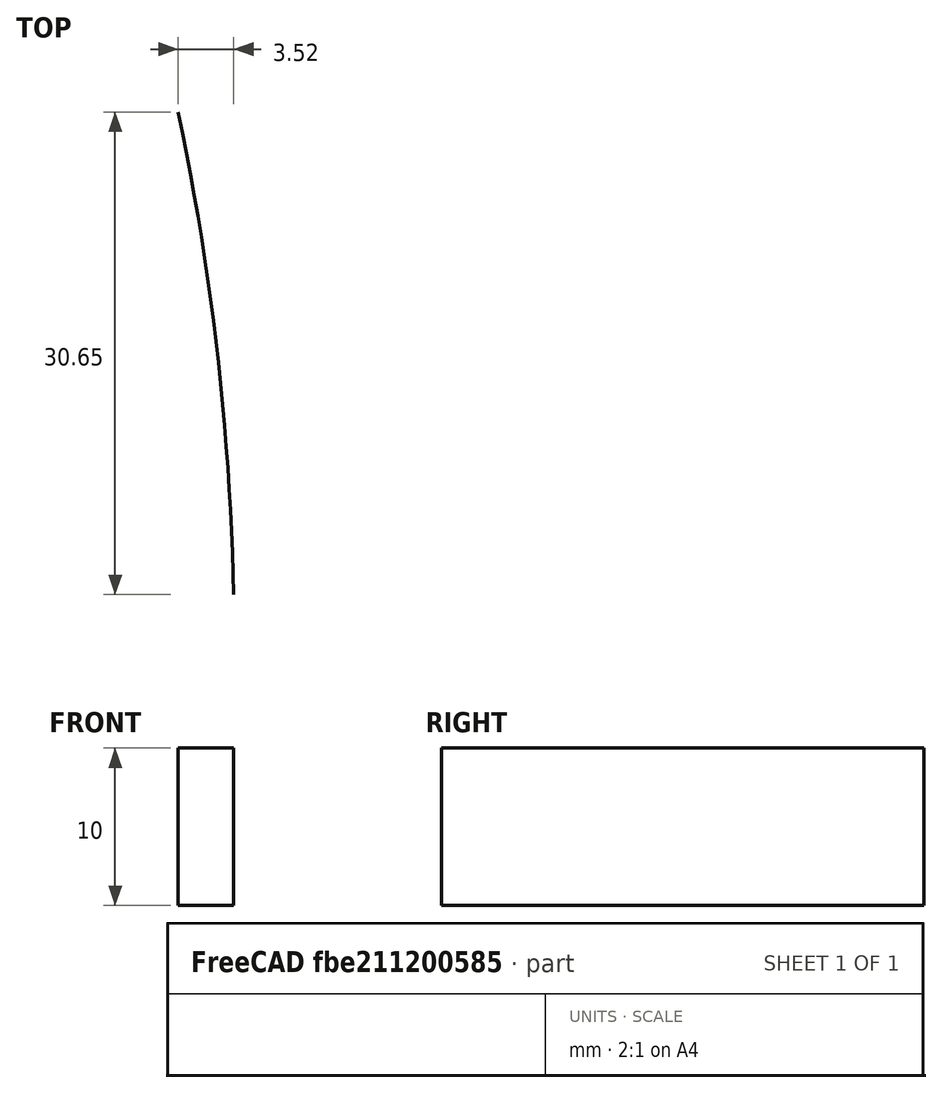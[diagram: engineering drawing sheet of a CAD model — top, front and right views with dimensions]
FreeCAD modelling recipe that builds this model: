
FCSTD DOCUMENT  (FreeCAD 0.21R33694 (Git))
Label: optics_test
License: All rights reserved
LicenseURL: http://en.wikipedia.org/wiki/All_rights_reserved
objects: Part::FeaturePython×3, Part::Extrusion×2, Sketcher::SketchObject×1
note: 6 computed .brp shape members not serialized (recipe doc carries the construction recipe); baked Part::Feature solids carry a one-line shape summary decoded from their .brp

FEATURE [Part::FeaturePython] Beam  # WARN: FeaturePython — macro-defined, semantics opaque (R4)
  BeamDistance = 0.2
  BeamNrColumns = 100
  BeamNrRows = 1
  ConeAngle = 360
  HideFirstPart = false
  MaxNrReflections = 200
  MaxRayLength = 1000000
  Order = 0
  Placement = pos=(0,0,0) rot=(0.125368,0.701528,0.701528;6.17151rad)
  Power = true
  Spherical = false
  Wavelength = 580
FEATURE [Sketcher::SketchObject] Sketch
  FullyConstrained = false
  sketch-geometry (3):
    g0: ArcOfParabola CenterX=65.2828 CenterY=1.74183 CenterZ=0 NormalX=0 NormalY=0 NormalZ=1 Focal=83.0288 AngleXU=-3.02781 StartAngle=-15.5186 EndAngle=15.3317
    g1: GeomPoint X=-17.2091 Y=-7.68525 Z=0
    g2: LineSegment StartX=65.2828 StartY=1.74183 StartZ=0 EndX=-17.2091 EndY=-7.68525 EndZ=0
  constraints (2):
    c: InternalAlignment(g1,g0)
    c: InternalAlignment(g2,g0)
FEATURE [Part::FeaturePython] Mirror001  # WARN: FeaturePython — macro-defined, semantics opaque (R4)
  Base = -> [Sketch]
  HitsFromBeam = 0
  OpticalType = 0
FEATURE [Part::Extrusion] Extrude
  Base = -> Sketch
  Dir = (0,0,1)
  DirMode = 2
  FaceMakerClass = Part::FaceMakerBullseye
  LengthFwd = 10
  LengthRev = 0
  Solid = false
  Symmetric = false
FEATURE [Part::Extrusion] Extrude001
  Base = -> Sketch
  Dir = (0,0,1)
  DirMode = 2
  FaceMakerClass = Part::FaceMakerBullseye
  LengthFwd = 10
  LengthRev = 0
  Solid = false
  Symmetric = false
FEATURE [Part::FeaturePython] Mirror  # WARN: FeaturePython — macro-defined, semantics opaque (R4)
  Base = -> [Extrude001]
  HitsFromBeam = 100
  OpticalType = 0
